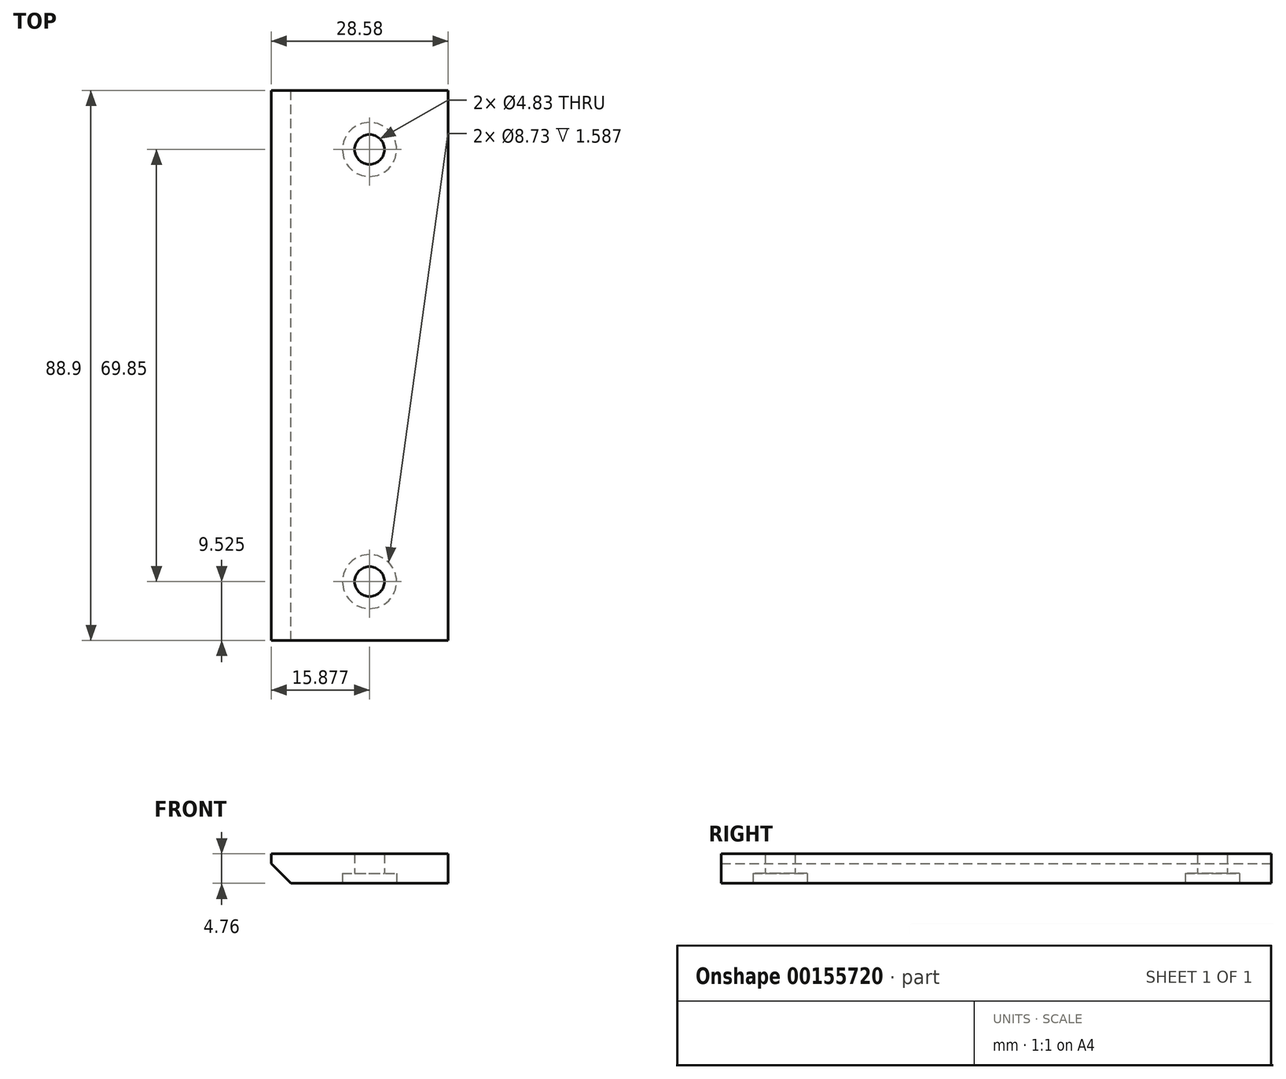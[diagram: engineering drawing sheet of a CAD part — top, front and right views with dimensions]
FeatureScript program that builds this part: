
annotation { "Feature Type Name" : "Feature", "Feature Type Description" : "" }
export const myFeature = defineFeature(function(context is Context, id is Id, definition is map)
    precondition{}
    {
        {
            var Q0;
            Q0=qCreatedBy(makeId("Front.planeOp"),FACE);
            var sketch = newSketch(context, id + "F2", { "sketchPlane" : qUnion([Q0])});
            skLineSegment(sketch, "E0", {"start": v(-14.29, 2.38) * mm, "end": v(-14.29, 0.8) * mm});
            skLineSegment(sketch, "E1", {"start": v(-14.29, 0.8) * mm, "end": v(-11.11, -2.38) * mm});
            skLineSegment(sketch, "E2", {"start": v(-11.11, -2.38) * mm, "end": v(14.29, -2.38) * mm});
            skLineSegment(sketch, "E3", {"start": v(14.29, -2.38) * mm, "end": v(14.29, 2.38) * mm});
            skLineSegment(sketch, "E4", {"start": v(14.29, 2.38) * mm, "end": v(-14.29, 2.38) * mm});
            skLineSegment(sketch, "E5", {"start": v(-14.29, 2.38) * mm, "end": v(14.29, -2.38) * mm, "construction": true});
            skSolve(sketch);
        }
        {
            var Q0;
            Q0 = qSketchRegion(id + "F2", true);
            extrude(context, id + "F0", {"entities" : qUnion([Q0]), "endBound" : BoundingType.SYMMETRIC, "depth" : 88.9 * mm});
        }
        {
            var Q0;
            Q0=makeQuery(id+"F0.opExtrude","SWEPT_FACE",FACE,{"disambiguationData":[OSD([sQuery(id+"F2.wireOp",EDGE,"E2")])]});
            var sketch = newSketch(context, id + "F3", { "sketchPlane" : qUnion([Q0])});
            skPoint(sketch, "E6", {"position": v(1.59, 34.93) * mm});
            skPoint(sketch, "E7", {"position": v(1.59, -34.93) * mm});
            skSolve(sketch);
        }
        {
            var Q0;
            Q0=sQuery(id+"F3.wireOp",VERTEX,"E6");
            var Q1;
            Q1=sQuery(id+"F3.wireOp",VERTEX,"E7");
            var Q2;
            Q2=makeQuery(id+"F0.opExtrude","SWEPT_BODY",BODY,{"disambiguationData":[OSD([sQuery(id+"F2.wireOp",EDGE,"E0"),sQuery(id+"F2.wireOp",EDGE,"E1"),sQuery(id+"F2.wireOp",EDGE,"E2"),sQuery(id+"F2.wireOp",EDGE,"E3"),sQuery(id+"F2.wireOp",EDGE,"E4")])]});
            hole(context, id + "F1", {"style" : HoleStyle.C_BORE, "endStyle" : HoleEndStyle.THROUGH, "holeDiameter" : 4.83 * mm, "cBoreDiameter" : 8.73 * mm, "cBoreDepth" : 1.59 * mm, "startFromSketch" : true, "locations" : qUnion([Q0, Q1]), "scope" : qUnion([Q2]), "isTappedThrough" : true});
        }
    });
